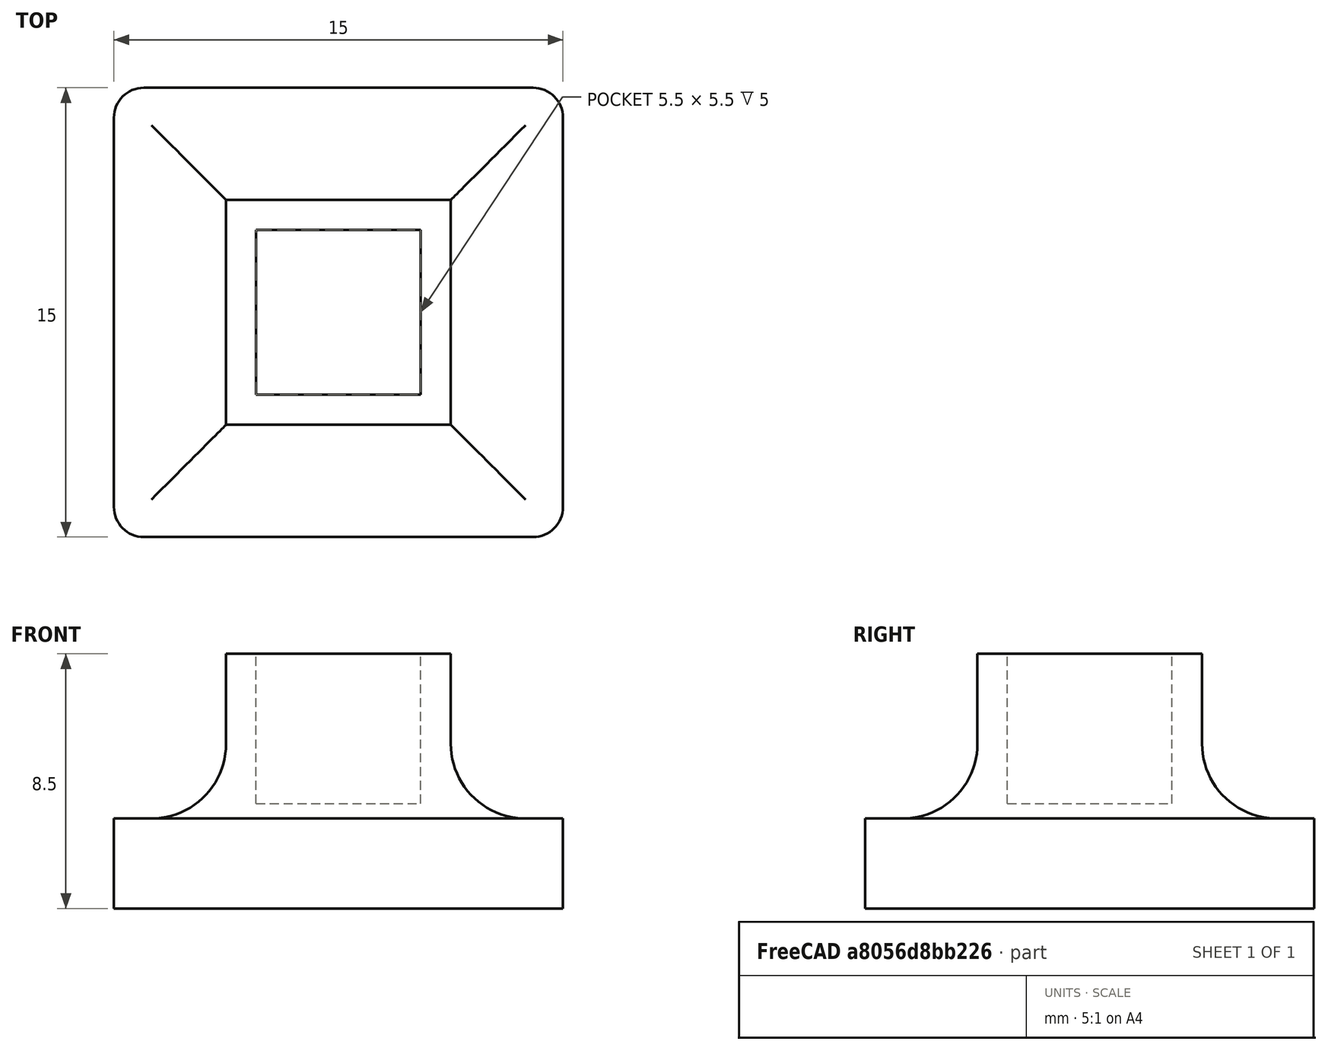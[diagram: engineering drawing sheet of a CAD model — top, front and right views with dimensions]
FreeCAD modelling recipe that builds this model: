
FCSTD DOCUMENT  (FreeCAD 0.15R4671 (Git))
Label: bootsV3
License: All rights reserved
LicenseURL: http://es.wikipedia.org/wiki/Todos_los_derechos_reservados
objects: Part::Box×4, Part::Cut×2, Part::Fillet×2, Mesh::Feature×1, Part::Feature×1, Part::MultiFuse×1
note: 10 computed .brp shape members not serialized (recipe doc carries the construction recipe); baked Part::Feature solids carry a one-line shape summary decoded from their .brp

FEATURE [Mesh::Feature] tibia_l
  Placement = pos=(-168,58,60) rot=(0,0,1;0rad)
FEATURE [Part::Box] Box  label="Cubo"
  Height = 94
  Length = 39
  Placement = pos=(147,-71,-41) rot=(0,0,1;0rad)
  Width = 29
FEATURE [Part::Feature] tibia_l001
  shape: bbox 16.26 x 20 x 99.69 mm, 2983 faces, 0 solids (baked)
FEATURE [Part::Cut] Cut
  Base = -> tibia_l001
  Tool = -> Box
FEATURE [Part::Box] Box001  label="inf"
  Height = 6
  Length = 5.5
  Placement = pos=(1,1,1) rot=(0,0,1;0rad)
  Width = 5.5
FEATURE [Part::Box] Box002  label="ext"
  Height = 6
  Length = 7.5
  Width = 7.5
FEATURE [Part::Box] Box003  label="Cube002"
  Height = 3
  Length = 15
  Placement = pos=(0,0,-2.5) rot=(0,0,1;0rad)
  Width = 15
FEATURE [Part::Cut] Cut001
  Base = -> Box002
  Placement = pos=(3.75,3.75,0) rot=(0,0,1;0rad)
  Tool = -> Box001
FEATURE [Part::MultiFuse] Fusion
  Shapes = -> [Cut001,Box003]
FEATURE [Part::Fillet] Fillet
  Base = -> Fusion
  Edges = 4 edges r=2.5: [Edge10,Edge11,Edge12,Edge13]
FEATURE [Part::Fillet] Fillet001
  Base = -> Fillet
  Edges = 4 edges r=1: [Edge17,Edge18,Edge21,Edge23]
